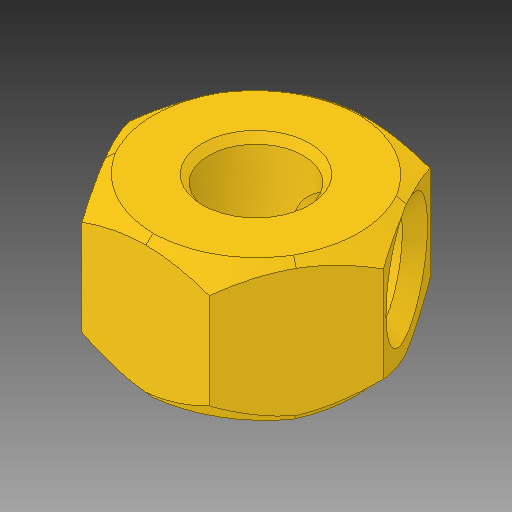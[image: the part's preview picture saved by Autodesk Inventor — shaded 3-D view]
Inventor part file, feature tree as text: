
AUTODESK INVENTOR PART (.ipt)
format: ipt  version: 2019.1 (Build 231200000, 200)  size: 157,696 bytes
history: mixed  units: in
note: dims shown in document units (in); Inventor stores cm internally (conversion verified against a paired STEP export)
features: fillet x1, imported_body x1
ambient origin geometry x8: Origin, YZ Plane, XZ Plane, XY Plane, X Axis, Y Axis, Z Axis, Center Point
bodies: Solid1 (imported_parasolid)
feature tree (2):
  fillet  "Fillet1"  [1 undecoded]
  imported_body  NMx_Import_Brep_tag  [imported B-rep: ~20 faces, bbox_mm=[5.863123, 4.5, 6.758657]]
note: 1 required parameter value undecoded (feature->parameter linkage not recoverable at this tier; creation-order binding heuristic only, values carry confidence <= 0.55)
